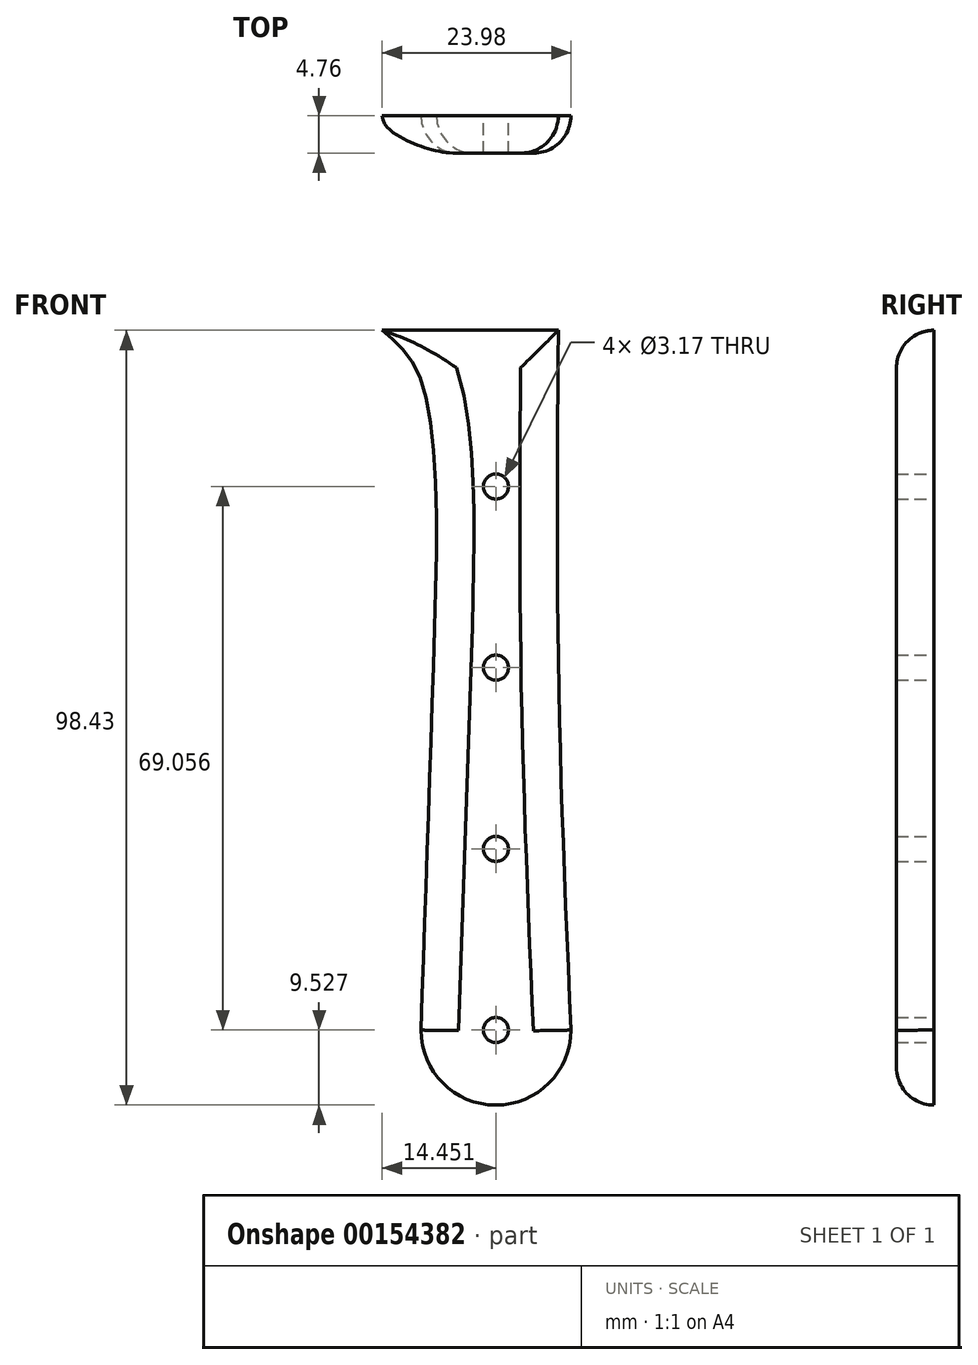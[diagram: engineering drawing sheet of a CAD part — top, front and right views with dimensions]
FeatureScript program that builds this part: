
annotation { "Feature Type Name" : "Feature", "Feature Type Description" : "" }
export const myFeature = defineFeature(function(context is Context, id is Id, definition is map)
    precondition{}
    {
        {
            var Q0;
            Q0=qCreatedBy(makeId("Front.planeOp"),FACE);
            var sketch = newSketch(context, id + "F0", { "sketchPlane" : qUnion([Q0])});
            skPoint(sketch, "E0", {"position": v(-13.22, 48.05) * mm});
            skPoint(sketch, "E1", {"position": v(9.17, 48.05) * mm});
            skLineSegment(sketch, "E2", {"start": v(-13.22, 48.05) * mm, "end": v(9.17, 48.05) * mm});
            skPoint(sketch, "E3", {"position": v(-8.3, 41.7) * mm});
            skPoint(sketch, "E4", {"position": v(-6.7, 5.18) * mm});
            skPoint(sketch, "E5", {"position": v(-8.3, -40.85) * mm});
            skPoint(sketch, "E6", {"position": v(9.17, 5.18) * mm});
            skPoint(sketch, "E7", {"position": v(10.76, -40.85) * mm});
            skPoint(sketch, "E8", {"position": v(1.23, -40.85) * mm});
            skPoint(sketch, "E9", {"position": v(1.23, -17.83) * mm});
            skPoint(sketch, "E10", {"position": v(1.23, 5.18) * mm});
            skPoint(sketch, "E11", {"position": v(1.23, 28.2) * mm});
            skFitSpline(sketch, "E12", {"points": [v(-13.22, 48.05) * mm, v(-8.3, 41.7) * mm, v(-6.7, 5.18) * mm, v(-8.3, -40.85) * mm], "startDerivative": vector(30.92, -25.24) * mm, "endDerivative": vector(-3.64, -103.8) * mm});
            skFitSpline(sketch, "E13", {"points": [v(9.17, 48.05) * mm, v(9.17, 5.18) * mm, v(10.76, -40.85) * mm], "startDerivative": vector(-0.77, -86.52) * mm, "endDerivative": vector(3.91, -91.25) * mm});
            skArc(sketch, "E14", {"start": v(-8.3, -40.85) * mm, "mid": v(1.23, -50.38) * mm, "end": v(10.76, -40.85) * mm});
            skPoint(sketch, "E15", {"position": v(1.23, -50.38) * mm});
            skSolve(sketch);
        }
        {
            var Q0;
            Q0=makeQuery(id+"F0.imprint","IMPRINT",FACE,{"disambiguationData":[TD([[makeQuery(id+"F0.imprint","IMPRINT",EDGE,{"derivedFrom":sQuery(id+"F0.wireOp",EDGE,"E2")}),-1.0]])]});
            extrude(context, id + "F2", {"entities" : qUnion([Q0]), "depth" : 4.76 * mm});
        }
        {
            var Q0;
            Q0=sQuery(id+"F0.wireOp",VERTEX,"E8");
            var Q1;
            Q1=sQuery(id+"F0.wireOp",VERTEX,"E9");
            var Q2;
            Q2=sQuery(id+"F0.wireOp",VERTEX,"E10");
            var Q3;
            Q3=sQuery(id+"F0.wireOp",VERTEX,"E11");
            var Q4;
            Q4=makeQuery(id+"F2.opExtrude","SWEPT_BODY",BODY,{"disambiguationData":[OSD([sQuery(id+"F0.wireOp",EDGE,"E2"),sQuery(id+"F0.wireOp",EDGE,"E12"),sQuery(id+"F0.wireOp",EDGE,"E13"),sQuery(id+"F0.wireOp",EDGE,"E14")])]});
            hole(context, id + "F1", {"style" : HoleStyle.SIMPLE, "endStyle" : HoleEndStyle.THROUGH, "oppositeDirection" : true, "holeDiameter" : 3.17 * mm, "locations" : qUnion([Q0, Q1, Q2, Q3]), "scope" : qUnion([Q4]), "isTappedThrough" : true});
        }
        {
            var Q0;
            Q0=makeQuery(id+"F2.opExtrude","CAP_EDGE",EDGE,{"disambiguationData":[OSD([sQuery(id+"F0.wireOp",EDGE,"E14")])],"isStart":false});
            var Q1;
            Q1=makeQuery(id+"F2.opExtrude","CAP_EDGE",EDGE,{"disambiguationData":[OSD([sQuery(id+"F0.wireOp",EDGE,"E12")])],"isStart":false});
            var Q2;
            Q2=makeQuery(id+"F2.opExtrude","CAP_EDGE",EDGE,{"disambiguationData":[OSD([sQuery(id+"F0.wireOp",EDGE,"E13")])],"isStart":false});
            var Q3;
            Q3=makeQuery(id+"F2.opExtrude","CAP_EDGE",EDGE,{"disambiguationData":[OSD([sQuery(id+"F0.wireOp",EDGE,"E2")])],"isStart":false});
            fillet(context, id + "F3", {"entities" : qUnion([Q0, Q1, Q2, Q3]), "radius" : 4.76 * mm, "tangentPropagation" : true, "allowEdgeOverflow" : false});
        }
    });
